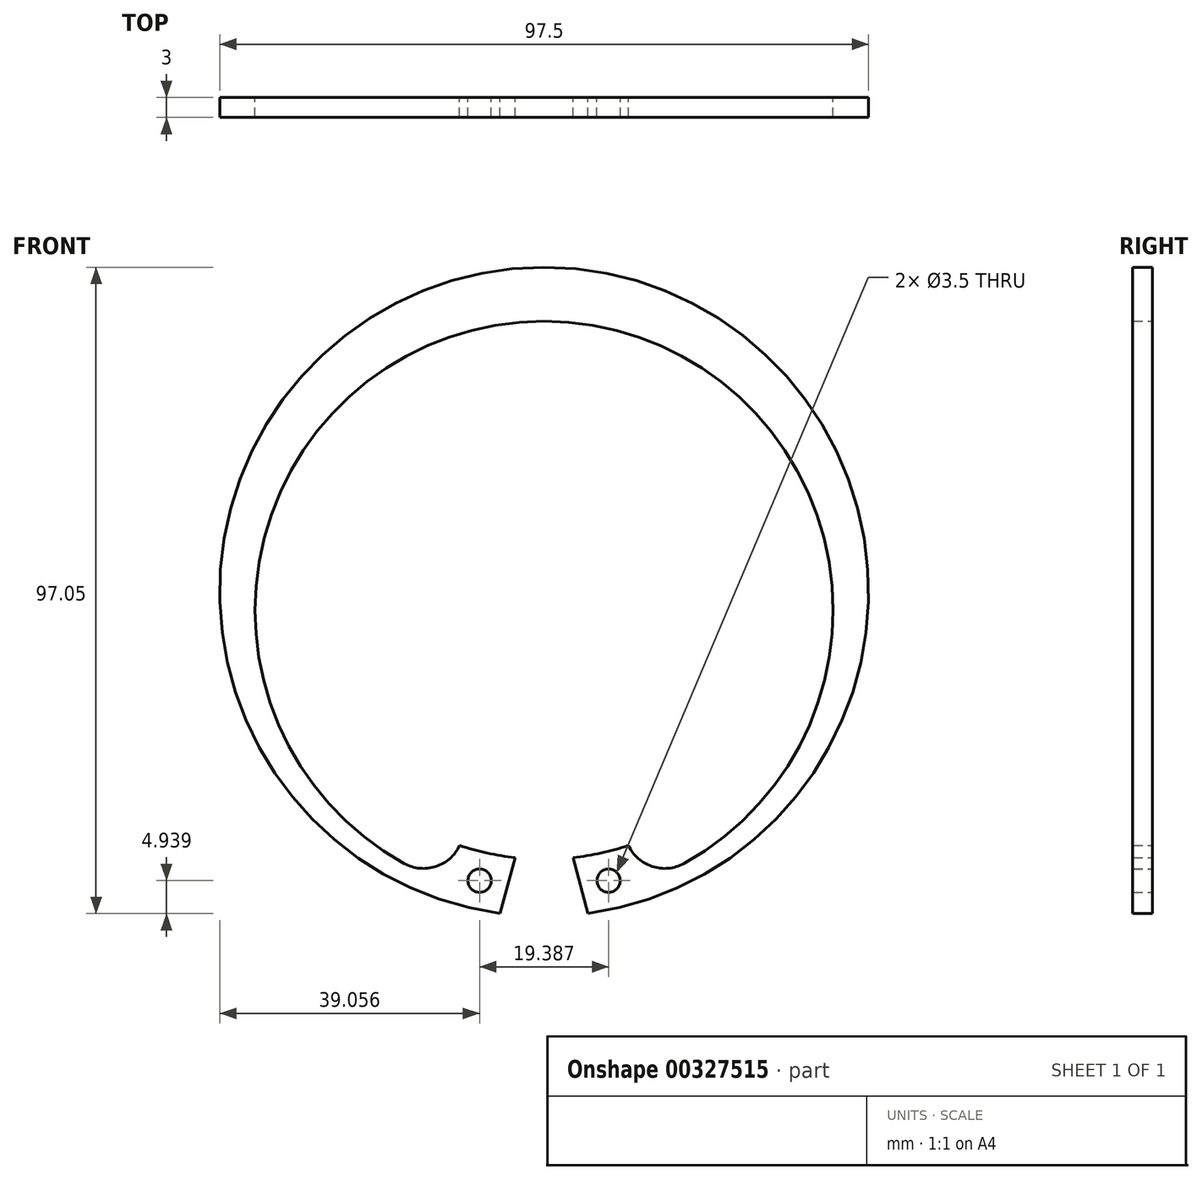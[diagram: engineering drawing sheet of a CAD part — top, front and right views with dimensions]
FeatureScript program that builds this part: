
annotation { "Feature Type Name" : "Feature", "Feature Type Description" : "" }
export const myFeature = defineFeature(function(context is Context, id is Id, definition is map)
    precondition{}
    {
        {
            var Q0;
            Q0=qCreatedBy(makeId("Front.planeOp"),FACE);
            var sketch = newSketch(context, id + "F0", { "sketchPlane" : qUnion([Q0])});
            skCircle(sketch, "E0", {"center": v(0, 0) * mm, "radius": 48.75 * mm});
            skLineSegment(sketch, "E1", {"start": v(6.6, -48.3) * mm, "end": v(4.35, -39.9) * mm});
            skLineSegment(sketch, "E2", {"start": v(-6.6, -48.3) * mm, "end": v(-4.35, -39.9) * mm});
            skLineSegment(sketch, "E3", {"start": v(-4.35, -39.9) * mm, "end": v(0, -39.9) * mm, "construction": true});
            skLineSegment(sketch, "E4", {"start": v(0, 0) * mm, "end": v(0, -39.9) * mm, "construction": true});
            skCircle(sketch, "E5", {"center": v(0, 0) * mm, "radius": 36.85 * mm, "construction": true});
            skLineSegment(sketch, "E6", {"start": v(0, 0) * mm, "end": v(0, 40.66) * mm, "construction": true});
            skLineSegment(sketch, "E7", {"start": v(0, 40.66) * mm, "end": v(0, 48.75) * mm, "construction": true});
            skCircle(sketch, "E8", {"center": v(9.7, -43.36) * mm, "radius": 1.75 * mm});
            skCircle(sketch, "E9", {"center": v(-9.7, -43.36) * mm, "radius": 1.75 * mm});
            skLineSegment(sketch, "E10", {"start": v(-9.7, -43.36) * mm, "end": v(-5.28, -43.36) * mm, "construction": true});
            skLineSegment(sketch, "E11", {"start": v(-55.06, -35.72) * mm, "end": v(0, -50.47) * mm, "construction": true});
            skLineSegment(sketch, "E12", {"start": v(0, -50.47) * mm, "end": v(0, -39.9) * mm, "construction": true});
            skLineSegment(sketch, "E13", {"start": v(0, -50.47) * mm, "end": v(59.37, -34.56) * mm, "construction": true});
            skLineSegment(sketch, "E14", {"start": v(0, -39.9) * mm, "end": v(4.35, -39.9) * mm, "construction": true});
            skCircle(sketch, "E15", {"center": v(0, 0) * mm, "radius": 40.13 * mm});
            skLineSegment(sketch, "E16", {"start": v(5.28, -43.36) * mm, "end": v(9.7, -43.36) * mm, "construction": true});
            skLineSegment(sketch, "E17", {"start": v(-9.7, -43.36) * mm, "end": v(-9.7, -38.95) * mm, "construction": true});
            skLineSegment(sketch, "E18", {"start": v(-9.7, -43.36) * mm, "end": v(-9.7, -45.11) * mm, "construction": true});
            skLineSegment(sketch, "E19", {"start": v(9.7, -43.36) * mm, "end": v(9.7, -38.95) * mm, "construction": true});
            skLineSegment(sketch, "E20", {"start": v(9.7, -43.36) * mm, "end": v(9.7, -47.78) * mm, "construction": true});
            skCircle(sketch, "E21", {"center": v(0, -2.77) * mm, "radius": 43.43 * mm});
            skLineSegment(sketch, "E22", {"start": v(-12.7, -38.07) * mm, "end": v(-14.93, -46.4) * mm});
            skLineSegment(sketch, "E23", {"start": v(12.7, -38.07) * mm, "end": v(14.93, -46.4) * mm});
            skLineSegment(sketch, "E24", {"start": v(9.7, -43.36) * mm, "end": v(14.1, -43.36) * mm, "construction": true});
            skLineSegment(sketch, "E25", {"start": v(-9.7, -43.36) * mm, "end": v(-14.1, -43.36) * mm, "construction": true});
            skLineSegment(sketch, "E26", {"start": v(-9.7, -45.11) * mm, "end": v(-9.7, -47.78) * mm, "construction": true});
            skSolve(sketch);
        }
        {
            var Q0;
            {var subQ6=sQuery(id+"F0.wireOp",EDGE,"E15");var subQ7=sQuery(id+"F0.wireOp",EDGE,"E2");var subQ8=makeQuery(id+"F0.imprint","INTERSECT",VERTEX,{"derivedFrom":[subQ7,subQ6]});Q0=makeQuery(id+"F0.imprint","IMPRINT",FACE,{"disambiguationData":[TD([[makeQuery(id+"F0.imprint","IMPRINT",EDGE,{"disambiguationData":[TD([[subQ8,1.0]])],"derivedFrom":subQ7}),1.0]])]});}
            var Q1;
            {var subQ6=sQuery(id+"F0.wireOp",EDGE,"E2");var subQ7=sQuery(id+"F0.wireOp",EDGE,"E0");var subQ8=makeQuery(id+"F0.imprint","INTERSECT",VERTEX,{"derivedFrom":[subQ7,subQ6]});Q1=makeQuery(id+"F0.imprint","IMPRINT",FACE,{"disambiguationData":[TD([[makeQuery(id+"F0.imprint","IMPRINT",EDGE,{"disambiguationData":[TD([[subQ8,1.0]])],"derivedFrom":subQ7}),1.0]])]});}
            var Q2;
            {var subQ0=sQuery(id+"F0.wireOp",EDGE,"E22");var subQ1=sQuery(id+"F0.wireOp",EDGE,"E0");var subQ2=makeQuery(id+"F0.imprint","INTERSECT",VERTEX,{"derivedFrom":[subQ1,subQ0]});Q2=makeQuery(id+"F0.imprint","IMPRINT",FACE,{"disambiguationData":[TD([[makeQuery(id+"F0.imprint","IMPRINT",EDGE,{"disambiguationData":[TD([[subQ2,1.0]])],"derivedFrom":subQ1}),1.0]])]});}
            var Q3;
            {var subQ0=sQuery(id+"F0.wireOp",EDGE,"E15");var subQ1=sQuery(id+"F0.wireOp",EDGE,"E1");var subQ2=makeQuery(id+"F0.imprint","INTERSECT",VERTEX,{"derivedFrom":[subQ1,subQ0]});Q3=makeQuery(id+"F0.imprint","IMPRINT",FACE,{"disambiguationData":[TD([[makeQuery(id+"F0.imprint","IMPRINT",EDGE,{"disambiguationData":[TD([[subQ2,1.0]])],"derivedFrom":subQ1}),-1.0]])]});}
            var Q4;
            {var subQ1=sQuery(id+"F0.wireOp",EDGE,"E1");var subQ6=sQuery(id+"F0.wireOp",EDGE,"E0");var subQ7=makeQuery(id+"F0.imprint","INTERSECT",VERTEX,{"derivedFrom":[subQ6,subQ1]});Q4=makeQuery(id+"F0.imprint","IMPRINT",FACE,{"disambiguationData":[TD([[makeQuery(id+"F0.imprint","IMPRINT",EDGE,{"disambiguationData":[TD([[subQ7,-1.0]])],"derivedFrom":subQ6}),1.0]])]});}
            extrude(context, id + "F1", {"entities" : qUnion([Q0, Q1, Q2, Q3, Q4]), "depth" : 3 * mm});
        }
        {
            var Q0;
            Q0=makeQuery(id+"F1.opExtrude","SWEPT_EDGE",EDGE,{"disambiguationData":[OSD([sQuery(id+"F0.wireOp",EDGE,"E21"),sQuery(id+"F0.wireOp",EDGE,"E23")])]});
            var Q1;
            Q1=makeQuery(id+"F1.opExtrude","SWEPT_EDGE",EDGE,{"disambiguationData":[OSD([sQuery(id+"F0.wireOp",EDGE,"E21"),sQuery(id+"F0.wireOp",EDGE,"E22")])]});
            fillet(context, id + "F2", {"entities" : qUnion([Q0, Q1]), "radius" : 5.98 * mm, "tangentPropagation" : true, "allowEdgeOverflow" : false});
        }
    });
